# Revit family: Toilet_Seat-Elongated_Closed_Front-KOHLER-Cachet-K-4636
name_source: partatom
category: Specialty Equipment
revit_build: Autodesk Revit 2015 (Build: 20140606_1530(x64)
units: mm (PartAtom-declared; Revit-internal decimal feet)

## types (10) — shared parameters
ADA Compliant = No
Assembly Code = C1030200
Date Modified = 12/17/2018
Default Elevation = 0"
Description = Elongated toilet seat
Height = 1 1/8"
Length = 18 1/16"
Manufacturer = KOHLER Co.
MasterFormat 1995 = 10820
MasterFormat 2004 = 10.28.13
Material = Plastic
Product Documentation Link = http://www.us.kohler.com
Product Name = Cachet
Product Page URL = http://www.us.kohler.com
URL = https://www.us.kohler.com
Width = 14 3/16"

## per-type parameters (varying)
| type | Finish | Model | Type |
| 0-White | Kohler-Plastic-0-White | K-4636-0 | 1 |
| 96-Biscuit | Kohler-Plastic-96-Biscuit | K-4636-96 | 2 |
| 47-Almond | Kohler-Plastic-47-Almond | K-4636-47 | 3 |
| NY-Dune | Kohler-Plastic-NY-Dune | K-4636-NY | 4 |
| 95-Ice Grey | Kohler-Plastic-95-Ice_Grey | K-4636-95 | 5 |
| G9-Sandbar | Kohler-Plastic-G9-Sandbar | K-4636-G9 | 6 |
| 33-Mexican Sand | Kohler-Plastic-33-Mexican_Sand | K-4636-33 | 7 |
| K4-Cashmere | Kohler-Plastic-K4-Cashmere | K-4636-K4 | 8 |
| 58-Thunder Grey | Kohler-Plastic-58-Thunder_Grey | K-4636-58 | 9 |
| 7-Black Black | Kohler-Plastic-7-Black_Black | K-4636-7 | 10 |

## geometry (parser evidence)
native form markers: Sweep x5
no freeform markers — native parametric forms only
